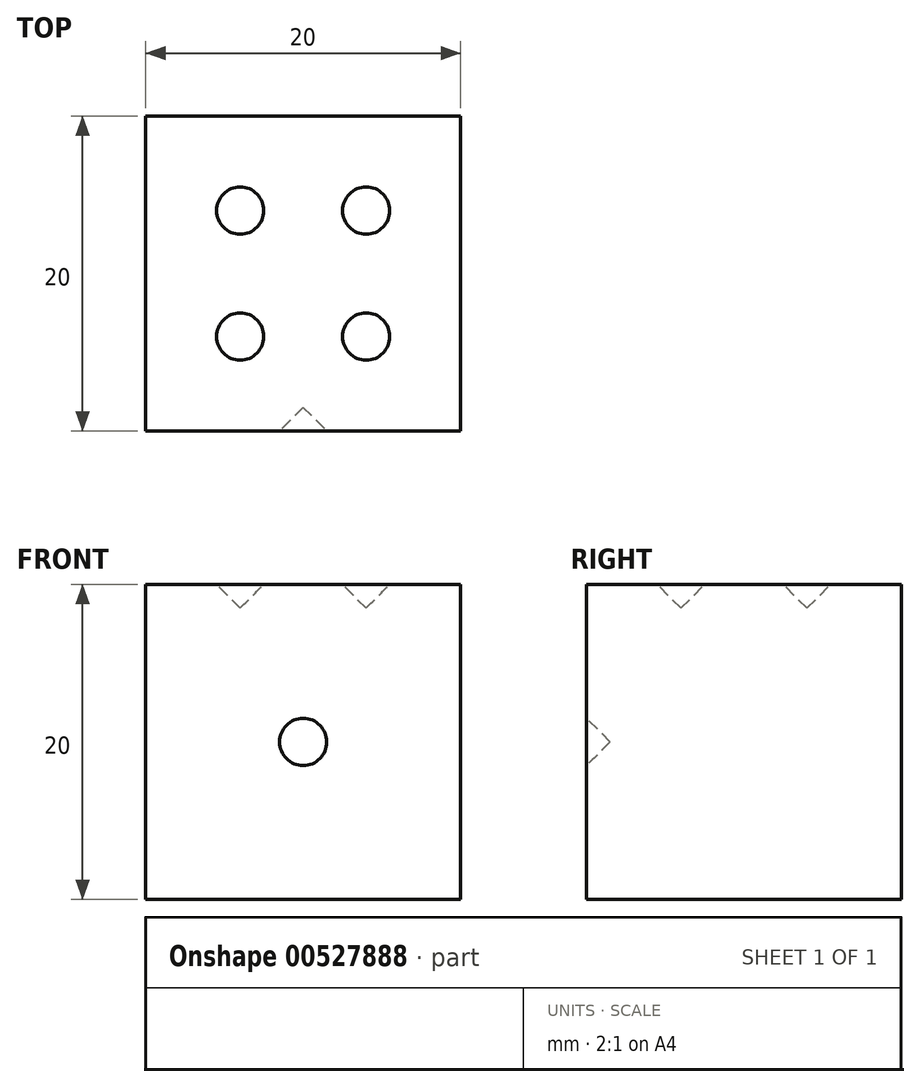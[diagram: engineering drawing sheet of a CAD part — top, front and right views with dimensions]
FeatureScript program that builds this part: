
annotation { "Feature Type Name" : "Feature", "Feature Type Description" : "" }
export const myFeature = defineFeature(function(context is Context, id is Id, definition is map)
    precondition{}
    {
        {
            var Q0;
            Q0=qCreatedBy(makeId("Top.planeOp"),FACE);
            var sketch = newSketch(context, id + "F0", { "sketchPlane" : qUnion([Q0])});
            skLineSegment(sketch, "E0.bottom", {"start": v(0, 0) * mm, "end": v(20, 0) * mm});
            skLineSegment(sketch, "E0.left", {"start": v(0, 0) * mm, "end": v(0, 20) * mm});
            skLineSegment(sketch, "E0.right", {"start": v(20, 0) * mm, "end": v(20, 20) * mm});
            skLineSegment(sketch, "E1", {"start": v(0, 20) * mm, "end": v(20, 20) * mm});
            skSolve(sketch);
        }
        {
            var Q0;
            Q0=qSketchRegion(id+"F0",true);
            extrude(context, id + "F1", {"entities" : qUnion([Q0]), "depth" : 20 * mm});
        }
        {
            var Q0;
            Q0=makeQuery(id+"F1.opExtrude","SWEPT_FACE",FACE,{"disambiguationData":[OSD([sQuery(id+"F0.wireOp",EDGE,"E0.bottom")])]});
            var sketch = newSketch(context, id + "F2", { "sketchPlane" : qUnion([Q0])});
            skLineSegment(sketch, "E2.0", {"start": v(0, 0) * mm, "end": v(20, 0) * mm, "construction": true});
            skLineSegment(sketch, "E2.1", {"start": v(0, 20) * mm, "end": v(20, 20) * mm, "construction": true});
            skLineSegment(sketch, "E3", {"start": v(10, 20) * mm, "end": v(10, 0) * mm, "construction": true});
            skCircle(sketch, "E4", {"center": v(10, 10) * mm, "radius": 1.5 * mm});
            skSolve(sketch);
        }
        {
            var Q0;
            Q0=makeQuery(id+"F2.imprint","IMPRINT",FACE,{"disambiguationData":[TD([[makeQuery(id+"F2.imprint","IMPRINT",EDGE,{"derivedFrom":sQuery(id+"F2.wireOp",EDGE,"E4")}),1.0]])]});
            extrude(context, id + "F3", {"entities" : qUnion([Q0]), "operationType" : NewBodyOperationType.REMOVE, "oppositeDirection" : true, "depth" : 1.5 * mm});
        }
        {
            var Q0;
            Q0=makeQuery(id+"F1.opExtrude","CAP_FACE",FACE,{"disambiguationData":[OSD([sQuery(id+"F0.wireOp",EDGE,"E0.bottom"),sQuery(id+"F0.wireOp",EDGE,"E0.left"),sQuery(id+"F0.wireOp",EDGE,"E0.right"),sQuery(id+"F0.wireOp",EDGE,"E1")])],"isStart":false});
            var sketch = newSketch(context, id + "F4", { "sketchPlane" : qUnion([Q0])});
            skLineSegment(sketch, "E5.0", {"start": v(0, 20) * mm, "end": v(6, 20) * mm, "construction": true});
            skLineSegment(sketch, "E6", {"start": v(6, 20) * mm, "end": v(6, 14) * mm, "construction": true});
            skCircle(sketch, "E7", {"center": v(6, 6) * mm, "radius": 1.5 * mm});
            skCircle(sketch, "E8", {"center": v(6, 14) * mm, "radius": 1.5 * mm});
            skPoint(sketch, "E9.orphan", {"position": v(20, 20) * mm});
            skPoint(sketch, "E10.orphan", {"position": v(20, 0) * mm});
            skLineSegment(sketch, "E11", {"start": v(0, 0) * mm, "end": v(6, 0) * mm, "construction": true});
            skLineSegment(sketch, "E12", {"start": v(6, 0) * mm, "end": v(6, 6) * mm, "construction": true});
            skLineSegment(sketch, "E13.0", {"start": v(0, 20) * mm, "end": v(20, 20) * mm, "construction": true});
            skLineSegment(sketch, "E13.1", {"start": v(0, 0) * mm, "end": v(20, 0) * mm, "construction": true});
            skLineSegment(sketch, "E14", {"start": v(10, 20) * mm, "end": v(10, 0) * mm, "construction": true});
            skCircle(sketch, "E15.MirrorC", {"center": v(14, 6) * mm, "radius": 1.5 * mm});
            skCircle(sketch, "E16.MirrorC", {"center": v(14, 14) * mm, "radius": 1.5 * mm});
            skSolve(sketch);
        }
        {
            var Q0;
            Q0=qSketchRegion(id+"F4",true);
            extrude(context, id + "F5", {"entities" : qUnion([Q0]), "operationType" : NewBodyOperationType.REMOVE, "oppositeDirection" : true, "depth" : 1.5 * mm});
        }
        {
            var Q0;
            Q0=makeQuery(id+"F3.boolean.opBoolean","COPY",EDGE,{"derivedFrom":makeQuery(id+"F3.opExtrude","CAP_EDGE",EDGE,{"disambiguationData":[OSD([sQuery(id+"F2.wireOp",EDGE,"E4")])],"isStart":false})});
            var Q1;
            Q1=makeQuery(id+"F5.boolean.opBoolean","COPY",EDGE,{"derivedFrom":makeQuery(id+"F5.opExtrude","CAP_EDGE",EDGE,{"disambiguationData":[OSD([sQuery(id+"F4.wireOp",EDGE,"E7")])],"isStart":false})});
            var Q2;
            Q2=makeQuery(id+"F5.boolean.opBoolean","COPY",EDGE,{"derivedFrom":makeQuery(id+"F5.opExtrude","CAP_EDGE",EDGE,{"disambiguationData":[OSD([sQuery(id+"F4.wireOp",EDGE,"E8")])],"isStart":false})});
            var Q3;
            Q3=makeQuery(id+"F5.boolean.opBoolean","COPY",EDGE,{"derivedFrom":makeQuery(id+"F5.opExtrude","CAP_EDGE",EDGE,{"disambiguationData":[OSD([sQuery(id+"F4.wireOp",EDGE,"E16.MirrorC")])],"isStart":false})});
            var Q4;
            Q4=makeQuery(id+"F5.boolean.opBoolean","COPY",EDGE,{"derivedFrom":makeQuery(id+"F5.opExtrude","CAP_EDGE",EDGE,{"disambiguationData":[OSD([sQuery(id+"F4.wireOp",EDGE,"E15.MirrorC")])],"isStart":false})});
            chamfer(context, id + "F6", {"entities" : qUnion([Q0, Q1, Q2, Q3, Q4]), "width" : 1.5 * mm, "tangentPropagation" : true});
        }
    });
